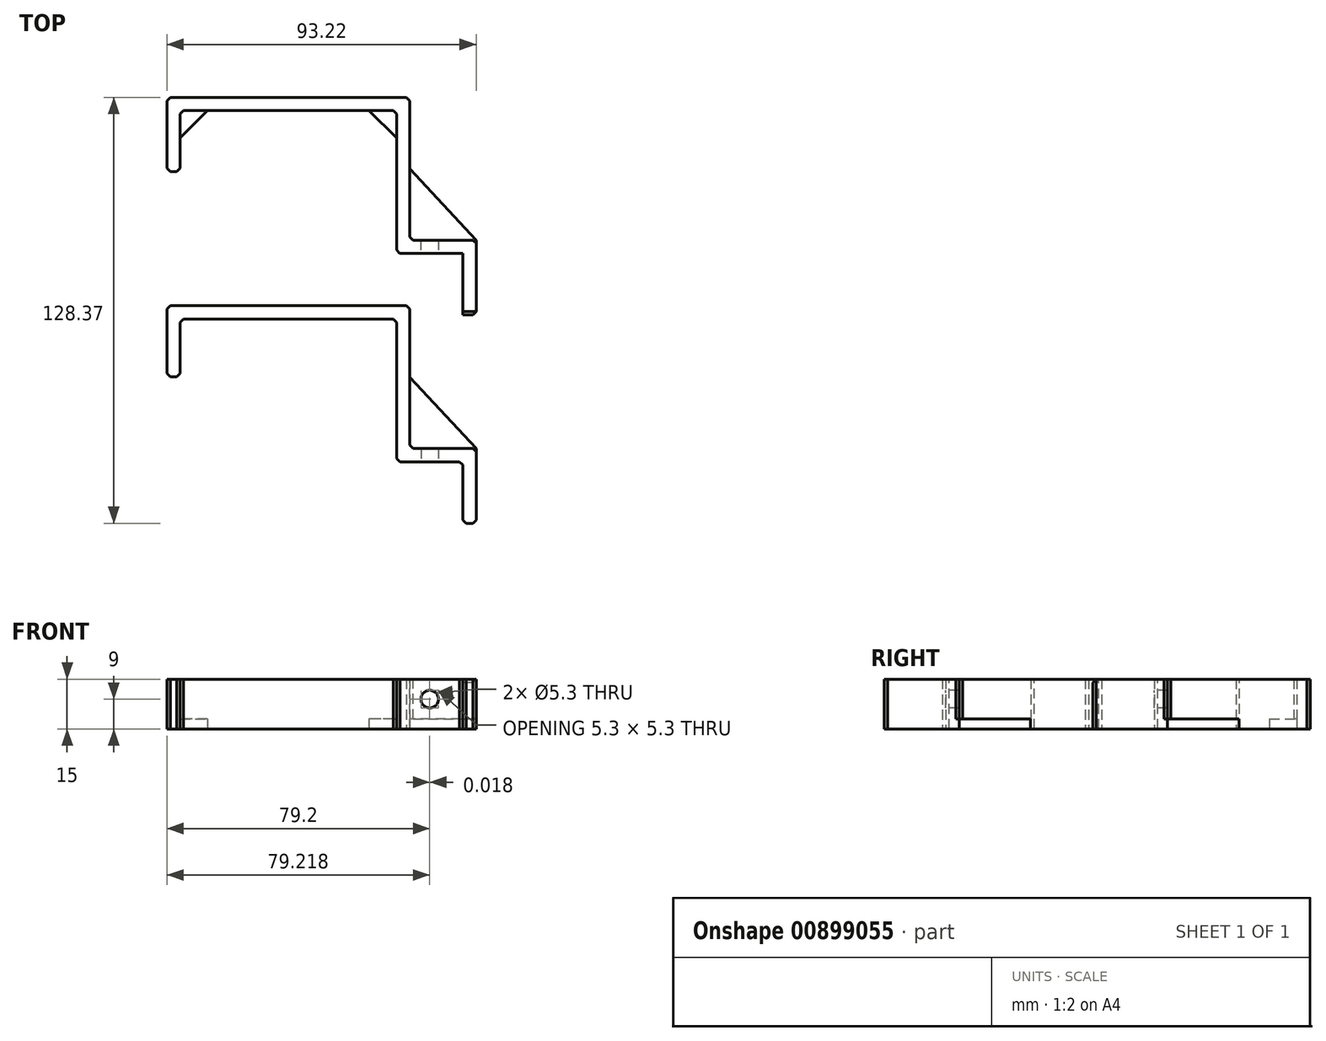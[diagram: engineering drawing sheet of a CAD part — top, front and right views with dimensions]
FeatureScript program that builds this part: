
annotation { "Feature Type Name" : "Feature", "Feature Type Description" : "" }
export const myFeature = defineFeature(function(context is Context, id is Id, definition is map)
    precondition{}
    {
        {
            var Q0;
            Q0=qCreatedBy(makeId("Top.planeOp"),FACE);
            var sketch = newSketch(context, id + "F0", { "sketchPlane" : qUnion([Q0])});
            skLineSegment(sketch, "E0", {"start": v(20, 1.43) * mm, "end": v(20, 20) * mm});
            skLineSegment(sketch, "E1", {"start": v(20, 20) * mm, "end": v(0, 20) * mm});
            skLineSegment(sketch, "E2", {"start": v(0, 20) * mm, "end": v(0, 63) * mm});
            skLineSegment(sketch, "E3", {"start": v(0, 63) * mm, "end": v(-65.2, 63) * mm});
            skLineSegment(sketch, "E4", {"start": v(-65.2, 63) * mm, "end": v(-65.2, 44.64) * mm});
            skLineSegment(sketch, "E5", {"start": v(-65.2, 44.64) * mm, "end": v(-69.2, 44.64) * mm});
            skLineSegment(sketch, "E6", {"start": v(-69.2, 44.64) * mm, "end": v(-69.2, 67) * mm});
            skLineSegment(sketch, "E7", {"start": v(-69.2, 67) * mm, "end": v(4, 67) * mm});
            skLineSegment(sketch, "E8", {"start": v(4, 67) * mm, "end": v(4, 24) * mm});
            skLineSegment(sketch, "E9", {"start": v(4, 24) * mm, "end": v(24, 24) * mm});
            skLineSegment(sketch, "E10", {"start": v(24, 24) * mm, "end": v(24, 1.43) * mm});
            skLineSegment(sketch, "E11", {"start": v(24, 1.43) * mm, "end": v(20, 1.43) * mm});
            skLineSegment(sketch, "E12", {"start": v(-4.31, 10) * mm, "end": v(48.4, 10) * mm, "construction": true});
            skLineSegment(sketch, "E13", {"start": v(-65.2, 54.75) * mm, "end": v(-56.95, 63) * mm});
            skLineSegment(sketch, "E14", {"start": v(0, 54.75) * mm, "end": v(-8.25, 63) * mm});
            skLineSegment(sketch, "E15", {"start": v(24, 24) * mm, "end": v(4, 45.5) * mm});
            skLineSegment(sketch, "E16", {"start": v(10, -9.79) * mm, "end": v(10, 50.66) * mm, "construction": true});
            skSolve(sketch);
        }
        {
            var Q0;
            Q0=makeQuery(id+"F0.imprint","IMPRINT",FACE,{"disambiguationData":[TD([[makeQuery(id+"F0.imprint","IMPRINT",EDGE,{"derivedFrom":sQuery(id+"F0.wireOp",EDGE,"E0")}),-1.0]])]});
            extrude(context, id + "F1", {"entities" : qUnion([Q0]), "depth" : 15 * mm, "offsetDistance" : 25 * mm});
        }
        {
            var Q0;
            {var subQ3=sQuery(id+"F0.wireOp",EDGE,"E13");Q0=makeQuery(id+"F0.imprint","IMPRINT",FACE,{"disambiguationData":[TD([[makeQuery(id+"F0.imprint","IMPRINT",EDGE,{"derivedFrom":subQ3}),1.0]])]});}
            var Q1;
            {var subQ3=sQuery(id+"F0.wireOp",EDGE,"E14");Q1=makeQuery(id+"F0.imprint","IMPRINT",FACE,{"disambiguationData":[TD([[makeQuery(id+"F0.imprint","IMPRINT",EDGE,{"derivedFrom":subQ3}),-1.0]])]});}
            var Q2;
            {var subQ0=sQuery(id+"F0.wireOp",EDGE,"E9");Q2=makeQuery(id+"F0.imprint","IMPRINT",FACE,{"disambiguationData":[TD([[makeQuery(id+"F0.imprint","IMPRINT",EDGE,{"derivedFrom":subQ0}),1.0]])]});}
            extrude(context, id + "F2", {"entities" : qUnion([Q0, Q1, Q2]), "operationType" : NewBodyOperationType.ADD, "depth" : 3 * mm, "offsetDistance" : 25 * mm});
        }
        {
            var Q0;
            Q0=makeQuery(id+"F1.opExtrude","SWEPT_EDGE",EDGE,{"disambiguationData":[OSD([sQuery(id+"F0.wireOp",EDGE,"E2"),sQuery(id+"F0.wireOp",EDGE,"E3")])]});
            var Q1;
            Q1=makeQuery(id+"F1.opExtrude","SWEPT_EDGE",EDGE,{"disambiguationData":[OSD([sQuery(id+"F0.wireOp",EDGE,"E3"),sQuery(id+"F0.wireOp",EDGE,"E4")])]});
            var Q2;
            Q2=makeQuery(id+"F1.opExtrude","SWEPT_EDGE",EDGE,{"disambiguationData":[OSD([sQuery(id+"F0.wireOp",EDGE,"E8"),sQuery(id+"F0.wireOp",EDGE,"E9")])]});
            var Q3;
            Q3=makeQuery(id+"F2.boolean.opBoolean","SPLIT",EDGE,{"derivedFrom":makeQuery(id+"F1.opExtrude","SWEPT_EDGE",EDGE,{"disambiguationData":[OSD([sQuery(id+"F0.wireOp",EDGE,"E9"),sQuery(id+"F0.wireOp",EDGE,"E10"),sQuery(id+"F0.wireOp",EDGE,"E15")])]})});
            var Q4;
            Q4=makeQuery(id+"F1.opExtrude","SWEPT_EDGE",EDGE,{"disambiguationData":[OSD([sQuery(id+"F0.wireOp",EDGE,"E7"),sQuery(id+"F0.wireOp",EDGE,"E8")])]});
            var Q5;
            Q5=makeQuery(id+"F1.opExtrude","SWEPT_EDGE",EDGE,{"disambiguationData":[OSD([sQuery(id+"F0.wireOp",EDGE,"E1"),sQuery(id+"F0.wireOp",EDGE,"E2")])]});
            var Q6;
            Q6=makeQuery(id+"F1.opExtrude","CAP_EDGE",EDGE,{"disambiguationData":[OSD([sQuery(id+"F0.wireOp",EDGE,"E11")])],"isStart":false});
            var Q7;
            Q7=makeQuery(id+"F1.opExtrude","SWEPT_EDGE",EDGE,{"disambiguationData":[OSD([sQuery(id+"F0.wireOp",EDGE,"E10"),sQuery(id+"F0.wireOp",EDGE,"E11")])]});
            var Q8;
            Q8=makeQuery(id+"F1.opExtrude","SWEPT_EDGE",EDGE,{"disambiguationData":[OSD([sQuery(id+"F0.wireOp",EDGE,"E6"),sQuery(id+"F0.wireOp",EDGE,"E7")])]});
            var Q9;
            Q9=makeQuery(id+"F1.opExtrude","SWEPT_EDGE",EDGE,{"disambiguationData":[OSD([sQuery(id+"F0.wireOp",EDGE,"E5"),sQuery(id+"F0.wireOp",EDGE,"E6")])]});
            var Q10;
            Q10=makeQuery(id+"F1.opExtrude","SWEPT_EDGE",EDGE,{"disambiguationData":[OSD([sQuery(id+"F0.wireOp",EDGE,"E4"),sQuery(id+"F0.wireOp",EDGE,"E5")])]});
            chamfer(context, id + "F3", {"entities" : qUnion([Q0, Q1, Q2, Q3, Q4, Q5, Q6, Q7, Q8, Q9, Q10]), "width" : 1 * mm, "tangentPropagation" : true});
        }
        {
            var Q0;
            Q0=makeQuery(id+"F1.opExtrude","SWEPT_FACE",FACE,{"disambiguationData":[OSD([sQuery(id+"F0.wireOp",EDGE,"E1")])]});
            var sketch = newSketch(context, id + "F4", { "sketchPlane" : qUnion([Q0])});
            skLineSegment(sketch, "E17", {"start": v(10, -3.88) * mm, "end": v(10, 21.9) * mm, "construction": true});
            skCircle(sketch, "E18", {"center": v(10, 9) * mm, "radius": 2.65 * mm});
            skSolve(sketch);
        }
        {
            var Q0;
            Q0=makeQuery(id+"F4.imprint","IMPRINT",FACE,{"disambiguationData":[TD([[makeQuery(id+"F4.imprint","IMPRINT",EDGE,{"derivedFrom":sQuery(id+"F4.wireOp",EDGE,"E18")}),1.0]])]});
            extrude(context, id + "F5", {"entities" : qUnion([Q0]), "operationType" : NewBodyOperationType.REMOVE, "oppositeDirection" : true, "depth" : 25 * mm, "offsetDistance" : 25 * mm});
        }
        {
            var Q0;
            Q0=qCreatedBy(makeId("Top.planeOp"),FACE);
            var sketch = newSketch(context, id + "F6", { "sketchPlane" : qUnion([Q0])});
            skLineSegment(sketch, "E19", {"start": v(20.02, -61.37) * mm, "end": v(20.02, -42.8) * mm});
            skLineSegment(sketch, "E20", {"start": v(20.02, -42.8) * mm, "end": v(0.02, -42.8) * mm});
            skLineSegment(sketch, "E21", {"start": v(0.02, -42.8) * mm, "end": v(0.02, 0.2) * mm});
            skLineSegment(sketch, "E22", {"start": v(0.02, 0.2) * mm, "end": v(-65.18, 0.2) * mm});
            skLineSegment(sketch, "E23", {"start": v(-65.18, 0.2) * mm, "end": v(-65.18, -17.16) * mm});
            skLineSegment(sketch, "E24", {"start": v(-65.18, -17.16) * mm, "end": v(-69.18, -17.16) * mm});
            skLineSegment(sketch, "E25", {"start": v(-69.18, -17.16) * mm, "end": v(-69.18, 4.2) * mm});
            skLineSegment(sketch, "E26", {"start": v(-69.18, 4.2) * mm, "end": v(4.02, 4.2) * mm});
            skLineSegment(sketch, "E27", {"start": v(4.02, 4.2) * mm, "end": v(4.02, -38.8) * mm});
            skLineSegment(sketch, "E28", {"start": v(4.02, -38.8) * mm, "end": v(24.02, -38.8) * mm});
            skLineSegment(sketch, "E29", {"start": v(24.02, -38.8) * mm, "end": v(24.02, -61.37) * mm});
            skLineSegment(sketch, "E30", {"start": v(24.02, -61.37) * mm, "end": v(20.02, -61.37) * mm});
            skLineSegment(sketch, "E31", {"start": v(-4.3, -52.8) * mm, "end": v(48.42, -52.8) * mm, "construction": true});
            skLineSegment(sketch, "E32", {"start": v(-65.18, -7.06) * mm, "end": v(-57.93, 0.2) * mm});
            skLineSegment(sketch, "E33", {"start": v(0.02, -7.06) * mm, "end": v(-7.24, 0.2) * mm});
            skLineSegment(sketch, "E34", {"start": v(24.02, -38.8) * mm, "end": v(4.02, -17.3) * mm});
            skLineSegment(sketch, "E35", {"start": v(10.02, -71.6) * mm, "end": v(10.02, -11.14) * mm, "construction": true});
            skSolve(sketch);
        }
        {
            var Q0;
            Q0=makeQuery(id+"F6.imprint","IMPRINT",FACE,{"disambiguationData":[TD([[makeQuery(id+"F6.imprint","IMPRINT",EDGE,{"derivedFrom":sQuery(id+"F6.wireOp",EDGE,"E19")}),-1.0]])]});
            extrude(context, id + "F7", {"entities" : qUnion([Q0]), "depth" : 15 * mm, "offsetDistance" : 25 * mm});
        }
        {
            var Q0;
            {var subQ0=sQuery(id+"F6.wireOp",EDGE,"E28");Q0=makeQuery(id+"F6.imprint","IMPRINT",FACE,{"disambiguationData":[TD([[makeQuery(id+"F6.imprint","IMPRINT",EDGE,{"derivedFrom":subQ0}),1.0]])]});}
            extrude(context, id + "F8", {"entities" : qUnion([Q0]), "operationType" : NewBodyOperationType.ADD, "depth" : 3 * mm, "offsetDistance" : 25 * mm});
        }
        {
            var Q0;
            Q0=makeQuery(id+"F7.opExtrude","SWEPT_FACE",FACE,{"disambiguationData":[OSD([sQuery(id+"F6.wireOp",EDGE,"E20")])]});
            var sketch = newSketch(context, id + "F9", { "sketchPlane" : qUnion([Q0])});
            skCircle(sketch, "E36", {"center": v(10.02, 9) * mm, "radius": 2.65 * mm});
            skSolve(sketch);
        }
        {
            var Q0;
            Q0=makeQuery(id+"F9.imprint","IMPRINT",FACE,{"disambiguationData":[TD([[makeQuery(id+"F9.imprint","IMPRINT",EDGE,{"derivedFrom":sQuery(id+"F9.wireOp",EDGE,"E36")}),1.0]])]});
            extrude(context, id + "F10", {"entities" : qUnion([Q0]), "operationType" : NewBodyOperationType.REMOVE, "oppositeDirection" : true, "depth" : 25 * mm, "offsetDistance" : 25 * mm});
        }
        {
            var Q0;
            Q0=makeQuery(id+"F7.opExtrude","SWEPT_EDGE",EDGE,{"disambiguationData":[OSD([sQuery(id+"F6.wireOp",EDGE,"E25"),sQuery(id+"F6.wireOp",EDGE,"E26")])]});
            var Q1;
            Q1=makeQuery(id+"F7.opExtrude","SWEPT_EDGE",EDGE,{"disambiguationData":[OSD([sQuery(id+"F6.wireOp",EDGE,"E24"),sQuery(id+"F6.wireOp",EDGE,"E25")])]});
            var Q2;
            Q2=makeQuery(id+"F7.opExtrude","SWEPT_EDGE",EDGE,{"disambiguationData":[OSD([sQuery(id+"F6.wireOp",EDGE,"E23"),sQuery(id+"F6.wireOp",EDGE,"E24")])]});
            var Q3;
            Q3=makeQuery(id+"F7.opExtrude","SWEPT_EDGE",EDGE,{"disambiguationData":[OSD([sQuery(id+"F6.wireOp",EDGE,"E22"),sQuery(id+"F6.wireOp",EDGE,"E23")])]});
            var Q4;
            Q4=makeQuery(id+"F7.opExtrude","SWEPT_EDGE",EDGE,{"disambiguationData":[OSD([sQuery(id+"F6.wireOp",EDGE,"E20"),sQuery(id+"F6.wireOp",EDGE,"E21")])]});
            var Q5;
            Q5=makeQuery(id+"F7.opExtrude","SWEPT_EDGE",EDGE,{"disambiguationData":[OSD([sQuery(id+"F6.wireOp",EDGE,"E26"),sQuery(id+"F6.wireOp",EDGE,"E27")])]});
            var Q6;
            Q6=makeQuery(id+"F7.opExtrude","SWEPT_EDGE",EDGE,{"disambiguationData":[OSD([sQuery(id+"F6.wireOp",EDGE,"E21"),sQuery(id+"F6.wireOp",EDGE,"E22")])]});
            var Q7;
            Q7=makeQuery(id+"F7.opExtrude","SWEPT_EDGE",EDGE,{"disambiguationData":[OSD([sQuery(id+"F6.wireOp",EDGE,"E27"),sQuery(id+"F6.wireOp",EDGE,"E28")])]});
            var Q8;
            Q8=makeQuery(id+"F8.boolean.opBoolean","SPLIT",EDGE,{"derivedFrom":makeQuery(id+"F7.opExtrude","SWEPT_EDGE",EDGE,{"disambiguationData":[OSD([sQuery(id+"F6.wireOp",EDGE,"E28"),sQuery(id+"F6.wireOp",EDGE,"E29"),sQuery(id+"F6.wireOp",EDGE,"E34")])]})});
            var Q9;
            Q9=makeQuery(id+"F7.opExtrude","SWEPT_EDGE",EDGE,{"disambiguationData":[OSD([sQuery(id+"F6.wireOp",EDGE,"E29"),sQuery(id+"F6.wireOp",EDGE,"E30")])]});
            var Q10;
            Q10=makeQuery(id+"F7.opExtrude","SWEPT_EDGE",EDGE,{"disambiguationData":[OSD([sQuery(id+"F6.wireOp",EDGE,"E19"),sQuery(id+"F6.wireOp",EDGE,"E30")])]});
            var Q11;
            Q11=makeQuery(id+"F7.opExtrude","SWEPT_EDGE",EDGE,{"disambiguationData":[OSD([sQuery(id+"F6.wireOp",EDGE,"E19"),sQuery(id+"F6.wireOp",EDGE,"E20")])]});
            chamfer(context, id + "F11", {"entities" : qUnion([Q0, Q1, Q2, Q3, Q4, Q5, Q6, Q7, Q8, Q9, Q10, Q11]), "width" : 1 * mm, "tangentPropagation" : true});
        }
    });
